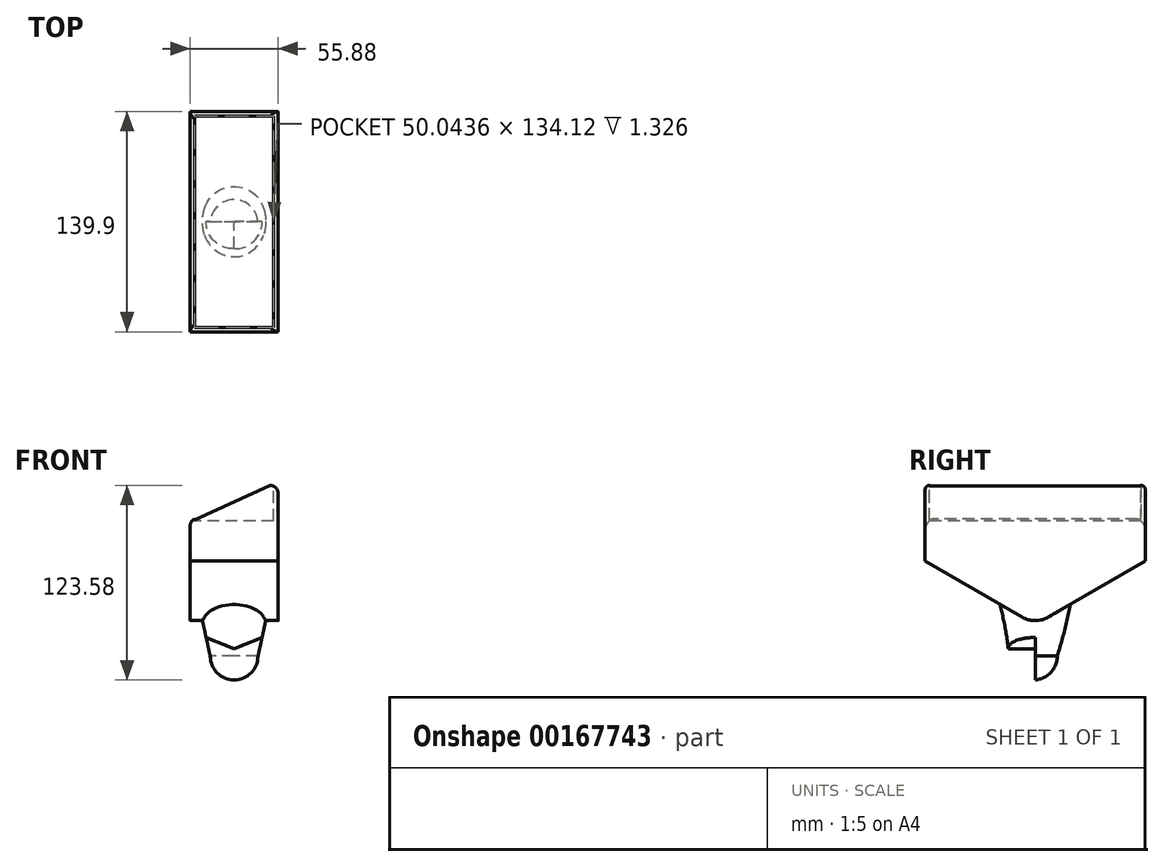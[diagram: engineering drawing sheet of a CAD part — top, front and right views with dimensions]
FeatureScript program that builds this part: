
annotation { "Feature Type Name" : "Feature", "Feature Type Description" : "" }
export const myFeature = defineFeature(function(context is Context, id is Id, definition is map)
    precondition{}
    {
        {
            var Q0;
            Q0=qCreatedBy(makeId("Top.planeOp"),FACE);
            var sketch = newSketch(context, id + "F0", { "sketchPlane" : qUnion([Q0])});
            skCircle(sketch, "E0", {"center": v(0, -1.17) * mm, "radius": 15.24 * mm});
            skSolve(sketch);
        }
        {
            var Q0;
            Q0=makeQuery(id+"F0.imprint","IMPRINT",FACE,{"disambiguationData":[TD([[makeQuery(id+"F0.imprint","IMPRINT",EDGE,{"derivedFrom":sQuery(id+"F0.wireOp",EDGE,"E0")}),1.0]])]});
            cPlane(context, id + "F1", {"entities" : qUnion([Q0]), "cplaneType" : CPlaneType.OFFSET, "offset" : 17.78 * mm, "width" : 152.4 * mm, "height" : 152.4 * mm});
        }
        {
            var Q0;
            Q0=qCreatedBy(id+"F1.planeOp",FACE);
            cPlane(context, id + "F2", {"entities" : qUnion([Q0]), "cplaneType" : CPlaneType.OFFSET, "offset" : 17.78 * mm, "width" : 152.4 * mm, "height" : 152.4 * mm});
        }
        {
            var Q0;
            Q0=qCreatedBy(id+"F1.planeOp",FACE);
            var sketch = newSketch(context, id + "F3", { "sketchPlane" : qUnion([Q0])});
            skCircle(sketch, "E1", {"center": v(0, 0) * mm, "radius": 19.05 * mm});
            skSolve(sketch);
        }
        {
            var Q0;
            Q0=qCreatedBy(id+"F2.planeOp",FACE);
            var sketch = newSketch(context, id + "F4", { "sketchPlane" : qUnion([Q0])});
            skCircle(sketch, "E2", {"center": v(0, 0) * mm, "radius": 22.86 * mm});
            skSolve(sketch);
        }
        {
            var Q0;
            Q0=makeQuery(id+"F0.imprint","IMPRINT",FACE,{"disambiguationData":[TD([[makeQuery(id+"F0.imprint","IMPRINT",EDGE,{"derivedFrom":sQuery(id+"F0.wireOp",EDGE,"E0")}),1.0]])]});
            var Q1;
            Q1=makeQuery(id+"F3.imprint","IMPRINT",FACE,{"disambiguationData":[TD([[makeQuery(id+"F3.imprint","IMPRINT",EDGE,{"derivedFrom":sQuery(id+"F3.wireOp",EDGE,"E1")}),1.0]])]});
            var Q2;
            Q2=makeQuery(id+"F4.imprint","IMPRINT",FACE,{"disambiguationData":[TD([[makeQuery(id+"F4.imprint","IMPRINT",EDGE,{"derivedFrom":sQuery(id+"F4.wireOp",EDGE,"E2")}),1.0]])]});
            loft(context, id + "F5", {"sheetProfilesArray" : [{ "sheetProfileEntities" : qUnion([Q0]) }, { "sheetProfileEntities" : qUnion([Q1]) }, { "sheetProfileEntities" : qUnion([Q2]) }]});
        }
        {
            var Q0;
            Q0=makeQuery(id+"F5.opLoft","CAP_FACE",FACE,{"disambiguationData":[OSD([makeQuery(id+"F0.imprint","IMPRINT",FACE,{"disambiguationData":[TD([[makeQuery(id+"F0.imprint","IMPRINT",EDGE,{"derivedFrom":sQuery(id+"F0.wireOp",EDGE,"E0")}),1.0]])]})])],"isStart":true});
            var sketch = newSketch(context, id + "F6", { "sketchPlane" : qUnion([Q0])});
            skLineSegment(sketch, "E3", {"start": v(0, 16.4) * mm, "end": v(0, -14.07) * mm});
            skArc(sketch, "E4", {"start": v(0, -14.07) * mm, "mid": v(15.17, 1.17) * mm, "end": v(0, 16.4) * mm});
            skSolve(sketch);
        }
        {
            var Q0;
            Q0=makeQuery(id+"F6.imprint","IMPRINT",FACE,{"disambiguationData":[TD([[makeQuery(id+"F6.imprint","IMPRINT",EDGE,{"derivedFrom":sQuery(id+"F6.wireOp",EDGE,"E3")}),1.0]])]});
            var Q1;
            Q1=sQuery(id+"F6.wireOp",EDGE,"E3");
            revolve(context, id + "F7", {"operationType" : NewBodyOperationType.ADD, "entities" : qUnion([Q0]), "axis" : qUnion([Q1]), "revolveType" : RevolveType.FULL});
        }
        {
            var Q0;
            Q0=qCreatedBy(makeId("Right.planeOp"),FACE);
            var sketch = newSketch(context, id + "F8", { "sketchPlane" : qUnion([Q0])});
            skLineSegment(sketch, "E5", {"start": v(-8.41, 24.8) * mm, "end": v(-61.77, 55.73) * mm});
            skLineSegment(sketch, "E6.MirrorCS", {"start": v(8.41, 24.8) * mm, "end": v(61.77, 55.73) * mm});
            skArc(sketch, "E7", {"start": v(-8.41, 24.8) * mm, "mid": v(0, 22.54) * mm, "end": v(8.41, 24.8) * mm});
            skLineSegment(sketch, "E8", {"start": v(0, 57.42) * mm, "end": v(0, 9.84) * mm});
            skLineSegment(sketch, "E9", {"start": v(-60.5, 60.47) * mm, "end": v(60.5, 60.47) * mm});
            skPoint(sketch, "E10.visualSharp", {"position": v(69.95, 60.47) * mm});
            skLineSegment(sketch, "E11", {"start": v(-61.77, 55.73) * mm, "end": v(-69.95, 60.47) * mm});
            skLineSegment(sketch, "E12", {"start": v(60.5, 60.47) * mm, "end": v(69.95, 60.47) * mm});
            skLineSegment(sketch, "E13", {"start": v(61.77, 55.73) * mm, "end": v(69.95, 60.47) * mm});
            skLineSegment(sketch, "E14.bottom", {"start": v(69.95, 60.47) * mm, "end": v(-69.95, 60.47) * mm});
            skSolve(sketch);
        }
        {
            var Q0;
            {var subQ4=sQuery(id+"F8.wireOp",EDGE,"E5");Q0=makeQuery(id+"F8.imprint","IMPRINT",FACE,{"disambiguationData":[TD([[makeQuery(id+"F8.imprint","IMPRINT",EDGE,{"derivedFrom":subQ4}),-1.0]])]});}
            extrude(context, id + "F9", {"entities" : qUnion([Q0]), "operationType" : NewBodyOperationType.ADD, "depth" : 27.94 * mm, "hasSecondDirection" : true, "secondDirectionOppositeDirection" : true, "secondDirectionDepth" : 27.94 * mm});
        }
        {
            var Q0;
            Q0=qCreatedBy(makeId("Front.planeOp"),FACE);
            var sketch = newSketch(context, id + "F10", { "sketchPlane" : qUnion([Q0])});
            skLineSegment(sketch, "E15", {"start": v(0, 0) * mm, "end": v(0, 60.46) * mm});
            skLineSegment(sketch, "E16.bottom", {"start": v(-27.94, 60.46) * mm, "end": v(27.94, 60.46) * mm});
            skLineSegment(sketch, "E16.top", {"start": v(-27.94, 60.46) * mm, "end": v(27.94, 60.46) * mm});
            skLineSegment(sketch, "E16.left", {"start": v(-27.94, 60.46) * mm, "end": v(-27.94, 60.46) * mm});
            skLineSegment(sketch, "E16.right", {"start": v(27.94, 60.46) * mm, "end": v(27.94, 60.46) * mm});
            skLineSegment(sketch, "E17.top", {"start": v(-27.94, 85.86) * mm, "end": v(27.94, 85.86) * mm});
            skLineSegment(sketch, "E17.left", {"start": v(-27.94, 60.46) * mm, "end": v(-27.94, 85.86) * mm});
            skLineSegment(sketch, "E17.right", {"start": v(27.94, 60.46) * mm, "end": v(27.94, 85.86) * mm});
            skLineSegment(sketch, "E18", {"start": v(27.94, 85.86) * mm, "end": v(27.94, 111.26) * mm});
            skLineSegment(sketch, "E19", {"start": v(27.94, 111.26) * mm, "end": v(-27.94, 85.86) * mm});
            skSolve(sketch);
        }
        {
            var Q0;
            Q0=makeQuery(id+"F10.imprint","IMPRINT",FACE,{"disambiguationData":[TD([[makeQuery(id+"F10.imprint","IMPRINT",EDGE,{"derivedFrom":sQuery(id+"F10.wireOp",EDGE,"E17.top")}),-1.0]])]});
            extrude(context, id + "F11", {"entities" : qUnion([Q0]), "operationType" : NewBodyOperationType.ADD, "depth" : 69.95 * mm, "hasSecondDirection" : true, "secondDirectionOppositeDirection" : true, "secondDirectionDepth" : 69.95 * mm});
        }
        {
            var Q0;
            Q0=makeQuery(id+"F10.imprint","IMPRINT",FACE,{"disambiguationData":[TD([[makeQuery(id+"F10.imprint","IMPRINT",EDGE,{"derivedFrom":sQuery(id+"F10.wireOp",EDGE,"E17.top")}),1.0]])]});
            extrude(context, id + "F12", {"entities" : qUnion([Q0]), "operationType" : NewBodyOperationType.ADD, "depth" : 69.95 * mm, "hasSecondDirection" : true, "secondDirectionOppositeDirection" : true, "secondDirectionDepth" : 69.95 * mm});
        }
        {
            var Q0;
            Q0=makeQuery(id+"F12.opExtrude","SWEPT_EDGE",EDGE,{"disambiguationData":[OSD([sQuery(id+"F10.wireOp",EDGE,"E18"),sQuery(id+"F10.wireOp",EDGE,"E19")])]});
            cPlane(context, id + "F13", {"entities" : qUnion([Q0]), "cplaneType" : CPlaneType.LINE_ANGLE, "offset" : 25.4 * mm, "angle" : 0 * degree, "width" : 152.4 * mm, "height" : 152.4 * mm});
        }
        {
            var Q0;
            Q0=qCreatedBy(id+"F13.planeOp",FACE);
            var sketch = newSketch(context, id + "F14", { "sketchPlane" : qUnion([Q0])});
            skLineSegment(sketch, "E20.bottom", {"start": v(25.02, 67.06) * mm, "end": v(-25.02, 67.06) * mm});
            skLineSegment(sketch, "E20.top", {"start": v(25.02, -67.06) * mm, "end": v(-25.02, -67.06) * mm});
            skLineSegment(sketch, "E20.left", {"start": v(25.02, 67.06) * mm, "end": v(25.02, -67.06) * mm});
            skLineSegment(sketch, "E20.right", {"start": v(-25.02, 67.06) * mm, "end": v(-25.02, -67.06) * mm});
            skPoint(sketch, "E20.middle", {"position": v(0, 0) * mm});
            skSolve(sketch);
        }
        {
            var Q0;
            Q0=makeQuery(id+"F14.imprint","IMPRINT",FACE,{"disambiguationData":[TD([[makeQuery(id+"F14.imprint","IMPRINT",EDGE,{"derivedFrom":sQuery(id+"F14.wireOp",EDGE,"E20.bottom")}),1.0]])]});
            extrude(context, id + "F15", {"entities" : qUnion([Q0]), "operationType" : NewBodyOperationType.REMOVE, "oppositeDirection" : true, "depth" : 25.4 * mm});
        }
        {
            var Q0;
            Q0=makeQuery(id+"F12.opExtrude","SWEPT_EDGE",EDGE,{"disambiguationData":[OSD([sQuery(id+"F10.wireOp",EDGE,"E18"),sQuery(id+"F10.wireOp",EDGE,"E19")])]});
            var Q1;
            {var subQ0=sQuery(id+"F10.wireOp",EDGE,"E19");var subQ1=sQuery(id+"F10.wireOp",EDGE,"E17.left");var subQ2=sQuery(id+"F10.wireOp",EDGE,"E17.top");Q1=makeQuery(id+"F12.boolean.opBoolean","MERGE",EDGE,{"derivedFrom":[makeQuery(id+"F11.opExtrude","SWEPT_EDGE",EDGE,{"disambiguationData":[OSD([subQ2,subQ1,subQ0])]}),makeQuery(id+"F12.opExtrude","SWEPT_EDGE",EDGE,{"disambiguationData":[OSD([subQ2,subQ1,subQ0])]})]});}
            var Q2;
            Q2=makeQuery(id+"F12.opExtrude","CAP_EDGE",EDGE,{"disambiguationData":[OSD([sQuery(id+"F10.wireOp",EDGE,"E19")])],"isStart":false});
            var Q3;
            Q3=makeQuery(id+"F12.opExtrude","CAP_EDGE",EDGE,{"disambiguationData":[OSD([sQuery(id+"F10.wireOp",EDGE,"E19")])],"isStart":true});
            fillet(context, id + "F16", {"entities" : qUnion([Q0, Q1, Q2, Q3]), "radius" : 5.08 * mm, "tangentPropagation" : true, "allowEdgeOverflow" : false});
        }
        {
            var Q0;
            Q0=qCreatedBy(makeId("Front.planeOp"),FACE);
            var sketch = newSketch(context, id + "F17", { "sketchPlane" : qUnion([Q0])});
            skLineSegment(sketch, "E21", {"start": v(-18.11, 11.97) * mm, "end": v(0, 4.73) * mm});
            skLineSegment(sketch, "E22.MirrorCS", {"start": v(18.11, 11.97) * mm, "end": v(0, 4.73) * mm});
            skLineSegment(sketch, "E23", {"start": v(-18.11, 11.97) * mm, "end": v(-18.11, -21.4) * mm});
            skLineSegment(sketch, "E24", {"start": v(-18.11, -21.4) * mm, "end": v(18.11, -21.4) * mm});
            skLineSegment(sketch, "E25", {"start": v(18.11, -21.4) * mm, "end": v(18.11, 11.97) * mm});
            skSolve(sketch);
        }
        {
            var Q0;
            Q0=makeQuery(id+"F17.imprint","IMPRINT",FACE,{"disambiguationData":[TD([[makeQuery(id+"F17.imprint","IMPRINT",EDGE,{"derivedFrom":sQuery(id+"F17.wireOp",EDGE,"E21")}),-1.0]])]});
            extrude(context, id + "F18", {"entities" : qUnion([Q0]), "operationType" : NewBodyOperationType.REMOVE, "depth" : 22.86 * mm});
        }
    });
